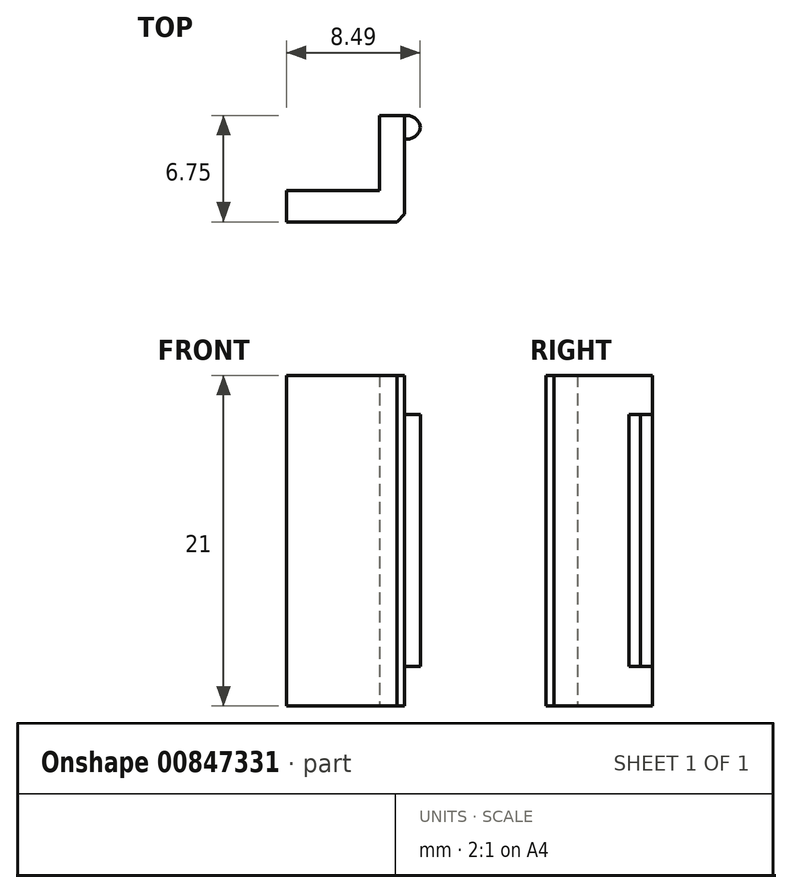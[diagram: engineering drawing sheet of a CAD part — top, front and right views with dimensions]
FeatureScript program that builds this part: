
annotation { "Feature Type Name" : "Feature", "Feature Type Description" : "" }
export const myFeature = defineFeature(function(context is Context, id is Id, definition is map)
    precondition{}
    {
        {
            var Q0;
            Q0=qCreatedBy(makeId("Top.planeOp"),FACE);
            var sketch = newSketch(context, id + "F0", { "sketchPlane" : qUnion([Q0])});
            skLineSegment(sketch, "E0", {"start": v(0, 0) * mm, "end": v(7.5, 0) * mm});
            skLineSegment(sketch, "E1", {"start": v(7.5, 0) * mm, "end": v(7.5, 5.25) * mm});
            skLineSegment(sketch, "E2", {"start": v(7.5, 5.25) * mm, "end": v(8.5, 5.25) * mm});
            skLineSegment(sketch, "E3", {"start": v(8.5, 5.25) * mm, "end": v(8.5, 6.75) * mm});
            skLineSegment(sketch, "E4", {"start": v(8.5, 6.75) * mm, "end": v(5.9, 6.75) * mm});
            skLineSegment(sketch, "E5", {"start": v(5.9, 6.75) * mm, "end": v(5.9, 2) * mm});
            skLineSegment(sketch, "E6", {"start": v(5.9, 2) * mm, "end": v(0, 2) * mm});
            skLineSegment(sketch, "E7", {"start": v(0, 2) * mm, "end": v(0, 0) * mm});
            skLineSegment(sketch, "E8", {"start": v(7.5, 5.25) * mm, "end": v(7.5, 6.75) * mm});
            skSolve(sketch);
        }
        {
            var Q0;
            Q0=makeQuery(id+"F0.imprint","IMPRINT",FACE,{"disambiguationData":[TD([[makeQuery(id+"F0.imprint","IMPRINT",EDGE,{"derivedFrom":sQuery(id+"F0.wireOp",EDGE,"E0")}),1.0]])]});
            extrude(context, id + "F1", {"entities" : qUnion([Q0]), "depth" : 21 * mm, "offsetDistance" : 25 * mm});
        }
        {
            var Q0;
            Q0=makeQuery(id+"F0.imprint","IMPRINT",FACE,{"disambiguationData":[TD([[makeQuery(id+"F0.imprint","IMPRINT",EDGE,{"derivedFrom":sQuery(id+"F0.wireOp",EDGE,"E2")}),1.0]])]});
            extrude(context, id + "F2", {"entities" : qUnion([Q0]), "operationType" : NewBodyOperationType.ADD, "depth" : 18.5 * mm, "offsetDistance" : 25 * mm, "hasSecondDirection" : true, "secondDirectionOppositeDirection" : false, "secondDirectionDepth" : 2.5 * mm});
        }
        {
            var Q0;
            Q0=makeQuery(id+"F1.opExtrude","SWEPT_EDGE",EDGE,{"disambiguationData":[OSD([sQuery(id+"F0.wireOp",EDGE,"E0"),sQuery(id+"F0.wireOp",EDGE,"E1")])]});
            chamfer(context, id + "F3", {"entities" : qUnion([Q0]), "width" : .5 * mm, "tangentPropagation" : true});
        }
        {
            var Q0;
            Q0=makeQuery(id+"F2.opExtrude","SWEPT_EDGE",EDGE,{"disambiguationData":[OSD([sQuery(id+"F0.wireOp",EDGE,"E3"),sQuery(id+"F0.wireOp",EDGE,"E4")])]});
            var Q1;
            Q1=makeQuery(id+"F2.opExtrude","SWEPT_EDGE",EDGE,{"disambiguationData":[OSD([sQuery(id+"F0.wireOp",EDGE,"E2"),sQuery(id+"F0.wireOp",EDGE,"E3")])]});
            fillet(context, id + "F4", {"entities" : qUnion([Q0, Q1]), "radius" : .85 * mm, "allowEdgeOverflow" : false});
        }
    });
